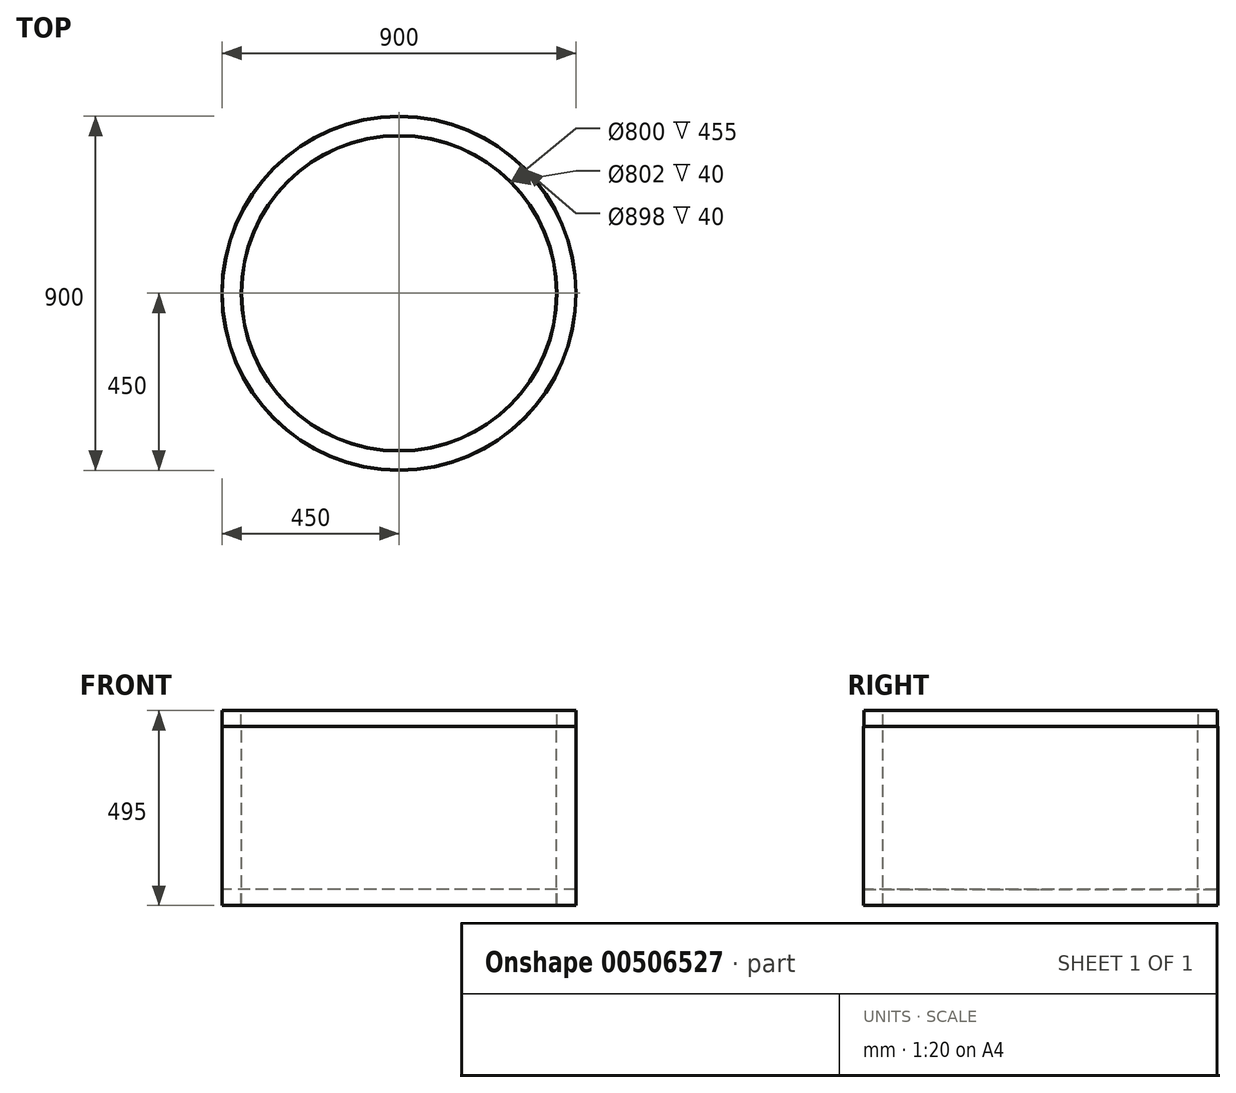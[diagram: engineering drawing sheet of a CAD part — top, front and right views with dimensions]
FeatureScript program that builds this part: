
annotation { "Feature Type Name" : "Feature", "Feature Type Description" : "" }
export const myFeature = defineFeature(function(context is Context, id is Id, definition is map)
    precondition{}
    {
        {
            var Q0;
            Q0=qCreatedBy(makeId("Front.planeOp"),FACE);
            var sketch = newSketch(context, id + "F0", { "sketchPlane" : qUnion([Q0])});
            skLineSegment(sketch, "E0", {"start": v(0, 74.87) * mm, "end": v(0, -73.71) * mm, "construction": true});
            skLineSegment(sketch, "E1", {"start": v(0, 374.84) * mm, "end": v(0, -528.94) * mm, "construction": true});
            skLineSegment(sketch, "E2", {"start": v(-400, -489.75) * mm, "end": v(-400, -34.75) * mm});
            skLineSegment(sketch, "E3", {"start": v(-400, -34.75) * mm, "end": v(-401, -34.75) * mm});
            skLineSegment(sketch, "E4", {"start": v(-401, -34.75) * mm, "end": v(-401, 5.25) * mm});
            skLineSegment(sketch, "E5", {"start": v(-401, 5.25) * mm, "end": v(-449, 5.25) * mm});
            skLineSegment(sketch, "E6", {"start": v(-449, 5.25) * mm, "end": v(-449, -34.75) * mm});
            skLineSegment(sketch, "E7", {"start": v(-449, -34.75) * mm, "end": v(-450, -34.75) * mm});
            skLineSegment(sketch, "E8", {"start": v(-450, -34.75) * mm, "end": v(-450, -489.75) * mm});
            skLineSegment(sketch, "E9", {"start": v(-450, -489.75) * mm, "end": v(-449, -489.75) * mm});
            skLineSegment(sketch, "E10", {"start": v(-449, -489.75) * mm, "end": v(-449, -449.75) * mm});
            skLineSegment(sketch, "E11", {"start": v(-449, -449.75) * mm, "end": v(-401, -449.75) * mm});
            skLineSegment(sketch, "E12", {"start": v(-401, -449.75) * mm, "end": v(-401, -489.75) * mm});
            skLineSegment(sketch, "E13", {"start": v(-401, -489.75) * mm, "end": v(-400, -489.75) * mm});
            skSolve(sketch);
        }
        {
            var Q0;
            Q0=qSketchRegion(id+"F0",true);
            var Q1;
            Q1=sQuery(id+"F0.wireOp",EDGE,"E1");
            revolve(context, id + "F1", {"entities" : qUnion([Q0]), "axis" : qUnion([Q1]), "revolveType" : RevolveType.FULL});
        }
    });
